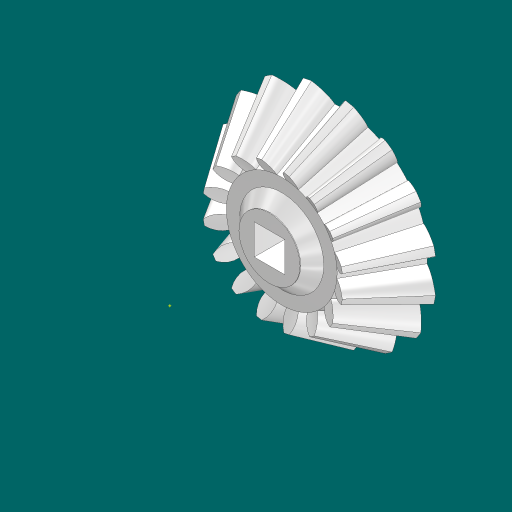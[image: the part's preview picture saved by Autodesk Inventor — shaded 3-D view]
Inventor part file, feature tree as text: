
AUTODESK INVENTOR PART (.ipt)
format: ipt  version: 2023.1 (Build 271208000, 208)  size: 530,944 bytes
history: native  units: mm
features: other x24, loft x2, pattern_circular x2, sketch x2, plane x2, extrude x2, chamfer x1
ambient origin geometry x6: Origin, XZ Plane, X Axis, Y Axis, Z Axis, Center Point
bodies: Solid1 (feature_tree)
feature tree (35):
  other  "Top Point"
  other  "Mesh Plane2"
  other  "Teeth Body"
  other  "Start Point"
  other  "Tooth Plane"
  other  "Start Sketch"
  other  "End Point"
  other  "3D Sketch Right"
  other  "End Plane Right"
  loft  "Loft Right"
  pattern_circular  "Circular Pattern Right"  [2 undecoded]
  other  "3D Sketch Left"
  other  "End Plane Left"
  loft  "Loft Left"
  pattern_circular  "Circular Pattern Left"  Angle=90.0deg  [1 undecoded]
  other  "Fix Body"
  sketch  "Sketch8"  dims[d2=22.50514mm d3=6.985mm d4=16.497551mm d5=90.0deg d7=3.516618mm d8=4.274671mm d9=10.495577mm d11=7.1247mm d12=2.259431mm d15=2.746481mm d16=6.743419mm d17=0.0mm d18=90.0deg d19=0.0mm d20=90.0deg d21=160.0mm d22=360.0deg d26=144.697709mm d27=6.129319mm d28=20.32mm d29=-5.349551mm d30=2.259431mm d31=2.746481mm d32=6.743419mm d35=0.0mm d37=0.0mm d39=0.0mm d40=90.0deg d41=160.0mm d42=360.0deg d46=90.0deg d47=90.0deg d48=0.0mm d49=0.0mm d50=90.0deg d51=1.963495mm d52=0.0mm d53=0.0mm d54=0.0mm d56=6.290752mm d57=13.91815mm d58=9.95067mm d59=8.942426mm d60=6.393316mm d61=8.942426mm d62=6.393316mm d63=90.0deg d64=90.0deg d65=144.697709mm d66=31.5mm d67=20.32mm d68=-5.349551mm d69=6.129319mm d70=2.746481mm d71=6.743419mm d72=2.259431mm d73=6.393316mm d74=8.942426mm d75=0.0mm d76=90.0deg d77=0.0mm d78=90.0deg d79=0.0mm d80=90.0deg d81=160.0mm d82=360.0deg d84=10.0mm d85=20.0mm d86=20.0mm d87=10.0mm d88=0.0mm d89=0.0mm d90=6.35mm d91=3.175mm d92=3.175mm d93=1.27mm d94=0.0mm d95=0.0mm d96=0.0mm d97=1.2mm d98=3.175mm d99=45.0deg]
  plane  "Work Plane6"
  plane  "Work Plane7"
  extrude  "Extrusion1"  Depth=3.175mm
  extrude  "Extrusion2"  Depth=3.175mm
  chamfer  "Chamfer1"  Distance=10.495577mm
  other  "Mesh Plane"
  other  "Top Plane"
  other  "Teeth Body Sketch"
  other  "End Plane"
  other  "End Sketch"
  other  "Helical Curve Left"
  other  "End Sketch Left"
  other  "Body Sketch"
  sketch  "Sketch6"  dims[d0=20.32mm d1=17.697832mm]
  other  "Srf1"
  other  "Helical Curve Right"
  other  "End Sketch Right"
  other  "Pitch Diameter"
note: 3 required parameter values undecoded (feature->parameter linkage not recoverable at this tier; creation-order binding heuristic only, values carry confidence <= 0.55)
